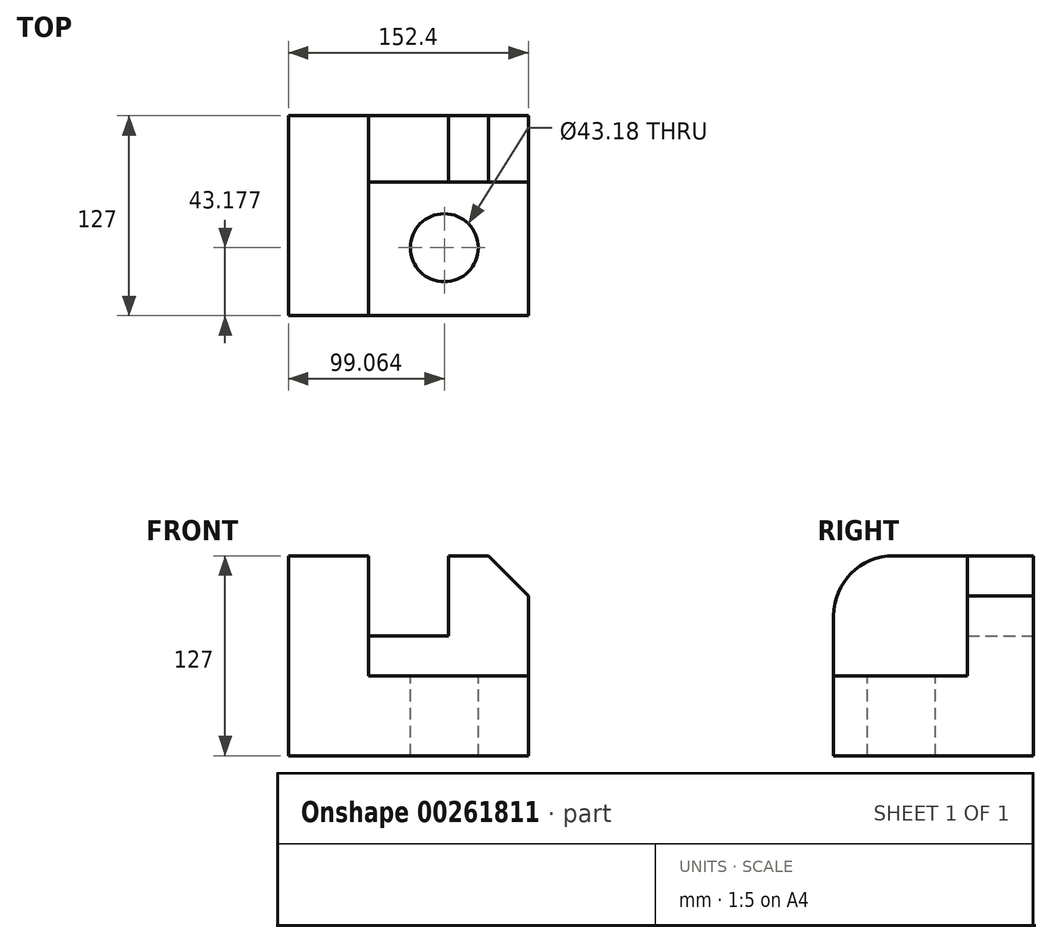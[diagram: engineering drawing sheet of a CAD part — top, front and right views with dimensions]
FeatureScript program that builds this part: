
annotation { "Feature Type Name" : "Feature", "Feature Type Description" : "" }
export const myFeature = defineFeature(function(context is Context, id is Id, definition is map)
    precondition{}
    {
        {
            var Q0;
            Q0=qCreatedBy(makeId("Top.planeOp"),FACE);
            var sketch = newSketch(context, id + "F0", { "sketchPlane" : qUnion([Q0])});
            skLineSegment(sketch, "E0.bottom", {"start": v(-75.1, 71.17) * mm, "end": v(77.3, 71.17) * mm});
            skLineSegment(sketch, "E0.top", {"start": v(-75.1, -55.83) * mm, "end": v(77.3, -55.83) * mm});
            skLineSegment(sketch, "E0.left", {"start": v(-75.1, 71.17) * mm, "end": v(-75.1, -55.83) * mm});
            skLineSegment(sketch, "E0.right", {"start": v(77.3, 71.17) * mm, "end": v(77.3, -55.83) * mm});
            skSolve(sketch);
        }
        {
            var Q0;
            Q0=makeQuery(id+"F0.imprint","IMPRINT",FACE,{"disambiguationData":[TD([[makeQuery(id+"F0.imprint","IMPRINT",EDGE,{"derivedFrom":sQuery(id+"F0.wireOp",EDGE,"E0.bottom")}),-1.0]])]});
            extrude(context, id + "F1", {"entities" : qUnion([Q0]), "depth" : 127 * mm});
        }
        {
            var Q0;
            Q0=makeQuery(id+"F1.opExtrude","CAP_FACE",FACE,{"disambiguationData":[OSD([sQuery(id+"F0.wireOp",EDGE,"E0.bottom"),sQuery(id+"F0.wireOp",EDGE,"E0.top"),sQuery(id+"F0.wireOp",EDGE,"E0.left"),sQuery(id+"F0.wireOp",EDGE,"E0.right")])],"isStart":false});
            var sketch = newSketch(context, id + "F2", { "sketchPlane" : qUnion([Q0])});
            skLineSegment(sketch, "E1.top", {"start": v(-24.3, 29.17) * mm, "end": v(26.5, 29.17) * mm});
            skLineSegment(sketch, "E2.bottom", {"start": v(-24.3, 29.17) * mm, "end": v(77.3, 29.17) * mm});
            skLineSegment(sketch, "E2.top", {"start": v(-24.3, -55.83) * mm, "end": v(77.3, -55.83) * mm});
            skLineSegment(sketch, "E2.left", {"start": v(-24.3, 29.17) * mm, "end": v(-24.3, -55.83) * mm});
            skLineSegment(sketch, "E2.right", {"start": v(77.3, 29.17) * mm, "end": v(77.3, -55.83) * mm});
            skSolve(sketch);
        }
        {
            var Q0;
            Q0=makeQuery(id+"F2.imprint","IMPRINT",FACE,{"disambiguationData":[TD([[makeQuery(id+"F2.imprint","IMPRINT",EDGE,{"derivedFrom":sQuery(id+"F2.wireOp",EDGE,"E2.top")}),1.0]])]});
            extrude(context, id + "F3", {"entities" : qUnion([Q0]), "operationType" : NewBodyOperationType.REMOVE, "oppositeDirection" : true, "depth" : 76.2 * mm});
        }
        {
            var Q0;
            Q0=makeQuery(id+"F1.opExtrude","CAP_FACE",FACE,{"disambiguationData":[OSD([sQuery(id+"F0.wireOp",EDGE,"E0.bottom"),sQuery(id+"F0.wireOp",EDGE,"E0.top"),sQuery(id+"F0.wireOp",EDGE,"E0.left"),sQuery(id+"F0.wireOp",EDGE,"E0.right")])],"isStart":false});
            var sketch = newSketch(context, id + "F4", { "sketchPlane" : qUnion([Q0])});
            skLineSegment(sketch, "E3.bottom", {"start": v(-24.3, 29.17) * mm, "end": v(26.5, 29.17) * mm});
            skLineSegment(sketch, "E3.top", {"start": v(-24.3, 71.17) * mm, "end": v(26.5, 71.17) * mm});
            skLineSegment(sketch, "E3.left", {"start": v(-24.3, 29.17) * mm, "end": v(-24.3, 71.17) * mm});
            skLineSegment(sketch, "E3.right", {"start": v(26.5, 29.17) * mm, "end": v(26.5, 71.17) * mm});
            skSolve(sketch);
        }
        {
            var Q0;
            Q0=makeQuery(id+"F4.imprint","IMPRINT",FACE,{"disambiguationData":[TD([[makeQuery(id+"F4.imprint","IMPRINT",EDGE,{"derivedFrom":sQuery(id+"F4.wireOp",EDGE,"E3.bottom")}),1.0]])]});
            extrude(context, id + "F5", {"entities" : qUnion([Q0]), "operationType" : NewBodyOperationType.REMOVE, "oppositeDirection" : true, "depth" : 50.8 * mm});
        }
        {
            var Q0;
            Q0=makeQuery(id+"F3.boolean.opBoolean","COPY",FACE,{"derivedFrom":makeQuery(id+"F3.opExtrude","CAP_FACE",FACE,{"disambiguationData":[OSD([sQuery(id+"F2.wireOp",EDGE,"E2.bottom"),sQuery(id+"F2.wireOp",EDGE,"E2.top"),sQuery(id+"F2.wireOp",EDGE,"E2.left"),sQuery(id+"F2.wireOp",EDGE,"E2.right")])],"isStart":false})});
            var sketch = newSketch(context, id + "F6", { "sketchPlane" : qUnion([Q0])});
            skCircle(sketch, "E4", {"center": v(23.95, -12.65) * mm, "radius": 21.6 * mm});
            skSolve(sketch);
        }
        {
            var Q0;
            Q0=makeQuery(id+"F1.opExtrude","CAP_EDGE",EDGE,{"disambiguationData":[OSD([sQuery(id+"F0.wireOp",EDGE,"E0.right")])],"isStart":false});
            chamfer(context, id + "F7", {"entities" : qUnion([Q0]), "width" : 25.4 * mm, "tangentPropagation" : true});
        }
        {
            var Q0;
            Q0=makeQuery(id+"F6.imprint","IMPRINT",FACE,{"disambiguationData":[TD([[makeQuery(id+"F6.imprint","IMPRINT",EDGE,{"derivedFrom":sQuery(id+"F6.wireOp",EDGE,"E4")}),1.0]])]});
            extrude(context, id + "F8", {"entities" : qUnion([Q0]), "operationType" : NewBodyOperationType.REMOVE, "endBound" : BoundingType.THROUGH_ALL, "oppositeDirection" : true, "depth" : 25.4 * mm});
        }
        {
            var Q0;
            Q0=makeQuery(id+"F1.opExtrude","CAP_EDGE",EDGE,{"disambiguationData":[OSD([sQuery(id+"F0.wireOp",EDGE,"E0.top")])],"isStart":false});
            fillet(context, id + "F9", {"entities" : qUnion([Q0]), "radius" : 38.1 * mm, "tangentPropagation" : true, "allowEdgeOverflow" : false});
        }
    });
